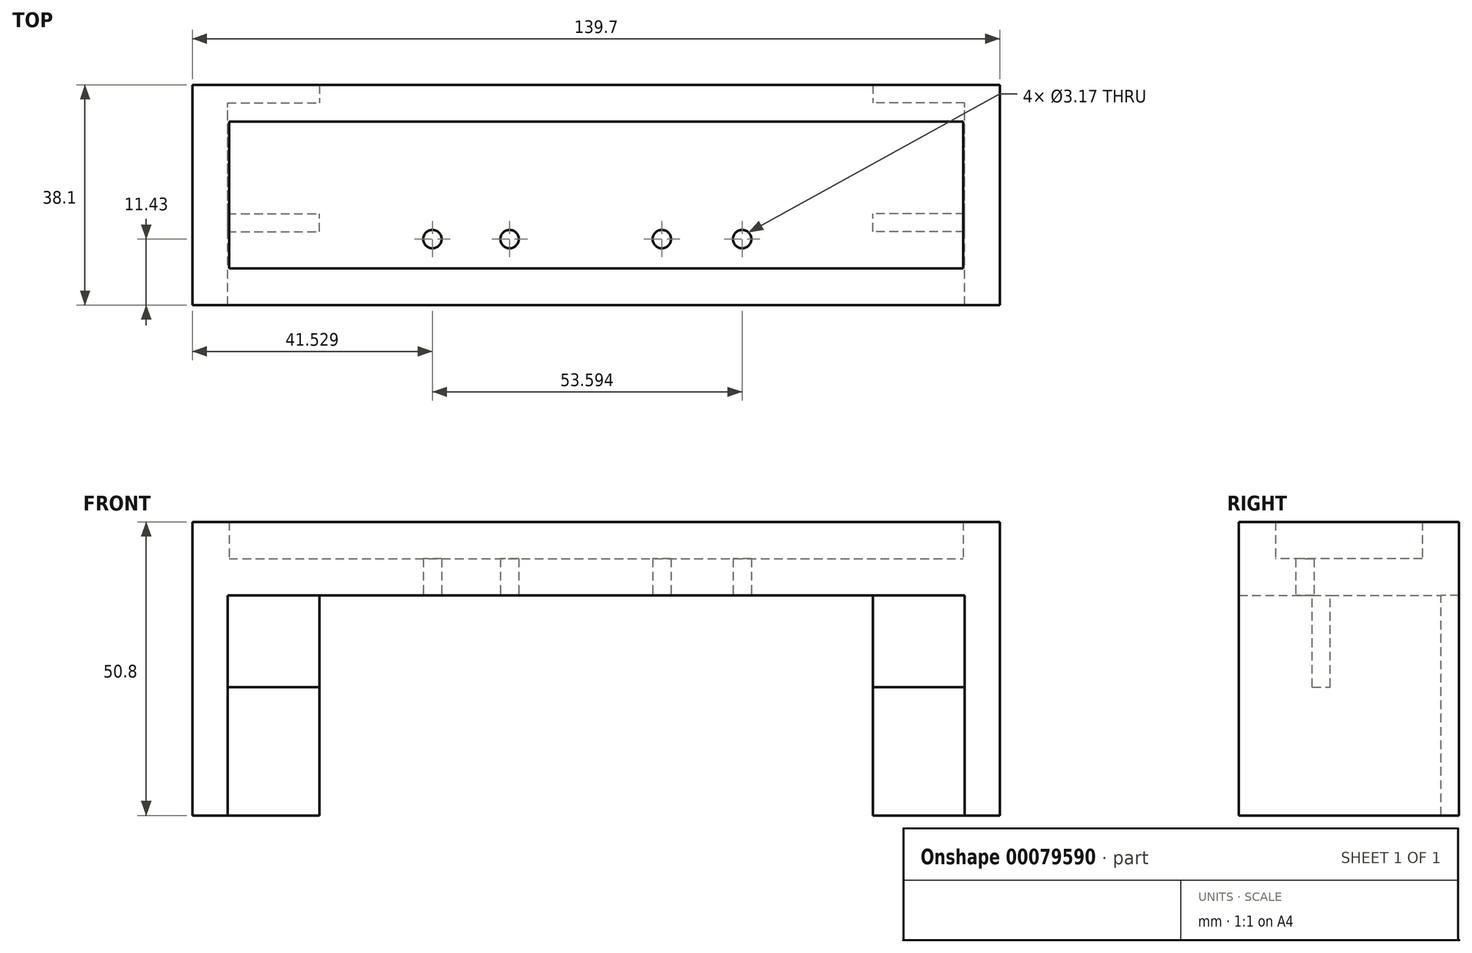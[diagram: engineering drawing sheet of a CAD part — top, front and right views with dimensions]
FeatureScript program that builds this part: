
annotation { "Feature Type Name" : "Feature", "Feature Type Description" : "" }
export const myFeature = defineFeature(function(context is Context, id is Id, definition is map)
    precondition{}
    {
        {
            var Q0;
            Q0=qCreatedBy(makeId("Top.planeOp"),FACE);
            var sketch = newSketch(context, id + "F0", { "sketchPlane" : qUnion([Q0])});
            skLineSegment(sketch, "E0.bottom", {"start": v(0, 0) * mm, "end": v(139.7, 0) * mm});
            skLineSegment(sketch, "E0.top", {"start": v(0, 38.1) * mm, "end": v(139.7, 38.1) * mm});
            skLineSegment(sketch, "E0.left", {"start": v(0, 0) * mm, "end": v(0, 38.1) * mm});
            skLineSegment(sketch, "E0.right", {"start": v(139.7, 0) * mm, "end": v(139.7, 38.1) * mm});
            skSolve(sketch);
        }
        {
            var Q0;
            Q0=makeQuery(id+"F0.imprint","IMPRINT",FACE,{"disambiguationData":[TD([[makeQuery(id+"F0.imprint","IMPRINT",EDGE,{"derivedFrom":sQuery(id+"F0.wireOp",EDGE,"E0.bottom")}),1.0]])]});
            extrude(context, id + "F1", {"entities" : qUnion([Q0]), "depth" : 6.35 * mm});
        }
        {
            var Q0;
            Q0=makeQuery(id+"F1.opExtrude","CAP_FACE",FACE,{"disambiguationData":[OSD([sQuery(id+"F0.wireOp",EDGE,"E0.bottom"),sQuery(id+"F0.wireOp",EDGE,"E0.top"),sQuery(id+"F0.wireOp",EDGE,"E0.left"),sQuery(id+"F0.wireOp",EDGE,"E0.right")])],"isStart":true});
            var sketch = newSketch(context, id + "F2", { "sketchPlane" : qUnion([Q0])});
            skLineSegment(sketch, "E1.bottom", {"start": v(0, 0) * mm, "end": v(6.1, 0) * mm});
            skLineSegment(sketch, "E1.top", {"start": v(0, -38.1) * mm, "end": v(6.1, -38.1) * mm});
            skLineSegment(sketch, "E1.left", {"start": v(0, 0) * mm, "end": v(0, -38.1) * mm});
            skLineSegment(sketch, "E1.right", {"start": v(6.1, -3.12) * mm, "end": v(6.1, -38.1) * mm});
            skLineSegment(sketch, "E2.bottom", {"start": v(139.7, 0) * mm, "end": v(133.6, 0) * mm});
            skLineSegment(sketch, "E2.top", {"start": v(139.7, -38.1) * mm, "end": v(133.6, -38.1) * mm});
            skLineSegment(sketch, "E2.left", {"start": v(139.7, 0) * mm, "end": v(139.7, -38.1) * mm});
            skLineSegment(sketch, "E2.right", {"start": v(133.6, 0) * mm, "end": v(133.6, -38.1) * mm});
            skLineSegment(sketch, "E3.left", {"start": v(6.1, 0) * mm, "end": v(6.1, -3.12) * mm});
            skLineSegment(sketch, "E4.bottom", {"start": v(133.6, -38.1) * mm, "end": v(117.73, -38.1) * mm});
            skLineSegment(sketch, "E4.top", {"start": v(133.6, -34.98) * mm, "end": v(117.73, -34.98) * mm});
            skLineSegment(sketch, "E4.left", {"start": v(133.6, -38.1) * mm, "end": v(133.6, -34.98) * mm});
            skLineSegment(sketch, "E4.right", {"start": v(117.73, -38.1) * mm, "end": v(117.73, -34.98) * mm});
            skLineSegment(sketch, "E5.bottom", {"start": v(6.1, -38.1) * mm, "end": v(21.97, -38.1) * mm});
            skLineSegment(sketch, "E5.top", {"start": v(6.1, -34.98) * mm, "end": v(21.97, -34.98) * mm});
            skLineSegment(sketch, "E5.left", {"start": v(6.1, -38.1) * mm, "end": v(6.1, -34.98) * mm});
            skLineSegment(sketch, "E5.right", {"start": v(21.97, -38.1) * mm, "end": v(21.97, -34.98) * mm});
            skLineSegment(sketch, "E6.bottom", {"start": v(6.1, -12.7) * mm, "end": v(21.97, -12.7) * mm});
            skLineSegment(sketch, "E6.top", {"start": v(6.1, -15.82) * mm, "end": v(21.97, -15.82) * mm});
            skLineSegment(sketch, "E6.left", {"start": v(6.1, -12.7) * mm, "end": v(6.1, -15.82) * mm});
            skLineSegment(sketch, "E6.right", {"start": v(21.97, -12.7) * mm, "end": v(21.97, -15.82) * mm});
            skLineSegment(sketch, "E7.bottom", {"start": v(133.6, -12.7) * mm, "end": v(117.73, -12.7) * mm});
            skLineSegment(sketch, "E7.top", {"start": v(133.6, -15.82) * mm, "end": v(117.73, -15.82) * mm});
            skLineSegment(sketch, "E7.left", {"start": v(133.6, -12.7) * mm, "end": v(133.6, -15.82) * mm});
            skLineSegment(sketch, "E7.right", {"start": v(117.73, -12.7) * mm, "end": v(117.73, -15.82) * mm});
            skSolve(sketch);
        }
        {
            var Q0;
            Q0=makeQuery(id+"F2.imprint","IMPRINT",FACE,{"disambiguationData":[TD([[makeQuery(id+"F2.imprint","IMPRINT",EDGE,{"derivedFrom":sQuery(id+"F2.wireOp",EDGE,"E5.bottom")}),1.0]])]});
            var Q1;
            Q1=makeQuery(id+"F2.imprint","IMPRINT",FACE,{"disambiguationData":[TD([[makeQuery(id+"F2.imprint","IMPRINT",EDGE,{"derivedFrom":sQuery(id+"F2.wireOp",EDGE,"E1.bottom")}),-1.0]])]});
            var Q2;
            Q2=makeQuery(id+"F2.imprint","IMPRINT",FACE,{"disambiguationData":[TD([[makeQuery(id+"F2.imprint","IMPRINT",EDGE,{"derivedFrom":sQuery(id+"F2.wireOp",EDGE,"E4.bottom")}),1.0]])]});
            var Q3;
            Q3=makeQuery(id+"F2.imprint","IMPRINT",FACE,{"disambiguationData":[TD([[makeQuery(id+"F2.imprint","IMPRINT",EDGE,{"derivedFrom":sQuery(id+"F2.wireOp",EDGE,"E2.bottom")}),-1.0]])]});
            extrude(context, id + "F3", {"entities" : qUnion([Q0, Q1, Q2, Q3]), "operationType" : NewBodyOperationType.ADD, "depth" : 38.1 * mm});
        }
        {
            var Q0;
            Q0=makeQuery(id+"F2.imprint","IMPRINT",FACE,{"disambiguationData":[TD([[makeQuery(id+"F2.imprint","IMPRINT",EDGE,{"derivedFrom":sQuery(id+"F2.wireOp",EDGE,"E6.bottom")}),-1.0]])]});
            extrude(context, id + "F4", {"entities" : qUnion([Q0]), "operationType" : NewBodyOperationType.ADD, "depth" : 15.88 * mm});
        }
        {
            var Q0;
            Q0=makeQuery(id+"F2.imprint","IMPRINT",FACE,{"disambiguationData":[TD([[makeQuery(id+"F2.imprint","IMPRINT",EDGE,{"derivedFrom":sQuery(id+"F2.wireOp",EDGE,"E7.bottom")}),1.0]])]});
            extrude(context, id + "F5", {"entities" : qUnion([Q0]), "operationType" : NewBodyOperationType.ADD, "depth" : 15.88 * mm});
        }
        {
            var Q0;
            Q0=makeQuery(id+"F1.opExtrude","CAP_FACE",FACE,{"disambiguationData":[OSD([sQuery(id+"F0.wireOp",EDGE,"E0.bottom"),sQuery(id+"F0.wireOp",EDGE,"E0.top"),sQuery(id+"F0.wireOp",EDGE,"E0.left"),sQuery(id+"F0.wireOp",EDGE,"E0.right")])],"isStart":false});
            var sketch = newSketch(context, id + "F6", { "sketchPlane" : qUnion([Q0])});
            skLineSegment(sketch, "E8.bottom", {"start": v(0, 38.1) * mm, "end": v(139.7, 38.1) * mm});
            skLineSegment(sketch, "E8.top", {"start": v(0, 0) * mm, "end": v(139.7, 0) * mm});
            skLineSegment(sketch, "E8.left", {"start": v(0, 38.1) * mm, "end": v(0, 0) * mm});
            skLineSegment(sketch, "E8.right", {"start": v(139.7, 38.1) * mm, "end": v(139.7, 0) * mm});
            skLineSegment(sketch, "E9.0", {"start": v(6.35, 31.75) * mm, "end": v(133.35, 31.75) * mm});
            skLineSegment(sketch, "E9.1", {"start": v(6.35, 31.75) * mm, "end": v(6.35, 6.35) * mm});
            skLineSegment(sketch, "E9.2", {"start": v(6.35, 6.35) * mm, "end": v(133.35, 6.35) * mm});
            skLineSegment(sketch, "E9.3", {"start": v(133.35, 31.75) * mm, "end": v(133.35, 6.35) * mm});
            skSolve(sketch);
        }
        {
            var Q0;
            Q0=makeQuery(id+"F6.imprint","IMPRINT",FACE,{"disambiguationData":[TD([[makeQuery(id+"F6.imprint","IMPRINT",EDGE,{"derivedFrom":sQuery(id+"F6.wireOp",EDGE,"E8.bottom")}),-1.0]])]});
            extrude(context, id + "F7", {"entities" : qUnion([Q0]), "operationType" : NewBodyOperationType.ADD, "depth" : 6.35 * mm});
        }
        {
            var Q0;
            {var subQ7=sQuery(id+"F2.wireOp",EDGE,"E3.left");Q0=makeQuery(id+"F2.imprint","IMPRINT",FACE,{"disambiguationData":[TD([[makeQuery(id+"F2.imprint","IMPRINT",EDGE,{"derivedFrom":subQ7}),1.0]])]});}
            var sketch = newSketch(context, id + "F8", { "sketchPlane" : qUnion([Q0])});
            skCircle(sketch, "E10", {"center": v(41.53, -11.43) * mm, "radius": 1.59 * mm});
            skCircle(sketch, "E11", {"center": v(54.89, -11.43) * mm, "radius": 1.59 * mm});
            skCircle(sketch, "E12", {"center": v(81.23, -11.43) * mm, "radius": 1.59 * mm});
            skCircle(sketch, "E13", {"center": v(95.12, -11.43) * mm, "radius": 1.59 * mm});
            skSolve(sketch);
        }
        {
            var Q0;
            Q0=makeQuery(id+"F8.imprint","IMPRINT",FACE,{"disambiguationData":[TD([[makeQuery(id+"F8.imprint","IMPRINT",EDGE,{"derivedFrom":sQuery(id+"F8.wireOp",EDGE,"E10")}),1.0]])]});
            var Q1;
            Q1=makeQuery(id+"F8.imprint","IMPRINT",FACE,{"disambiguationData":[TD([[makeQuery(id+"F8.imprint","IMPRINT",EDGE,{"derivedFrom":sQuery(id+"F8.wireOp",EDGE,"E11")}),1.0]])]});
            var Q2;
            Q2=makeQuery(id+"F8.imprint","IMPRINT",FACE,{"disambiguationData":[TD([[makeQuery(id+"F8.imprint","IMPRINT",EDGE,{"derivedFrom":sQuery(id+"F8.wireOp",EDGE,"E12")}),1.0]])]});
            var Q3;
            Q3=makeQuery(id+"F8.imprint","IMPRINT",FACE,{"disambiguationData":[TD([[makeQuery(id+"F8.imprint","IMPRINT",EDGE,{"derivedFrom":sQuery(id+"F8.wireOp",EDGE,"E13")}),1.0]])]});
            extrude(context, id + "F9", {"entities" : qUnion([Q0, Q1, Q2, Q3]), "operationType" : NewBodyOperationType.REMOVE, "oppositeDirection" : true, "depth" : 25.4 * mm});
        }
    });
